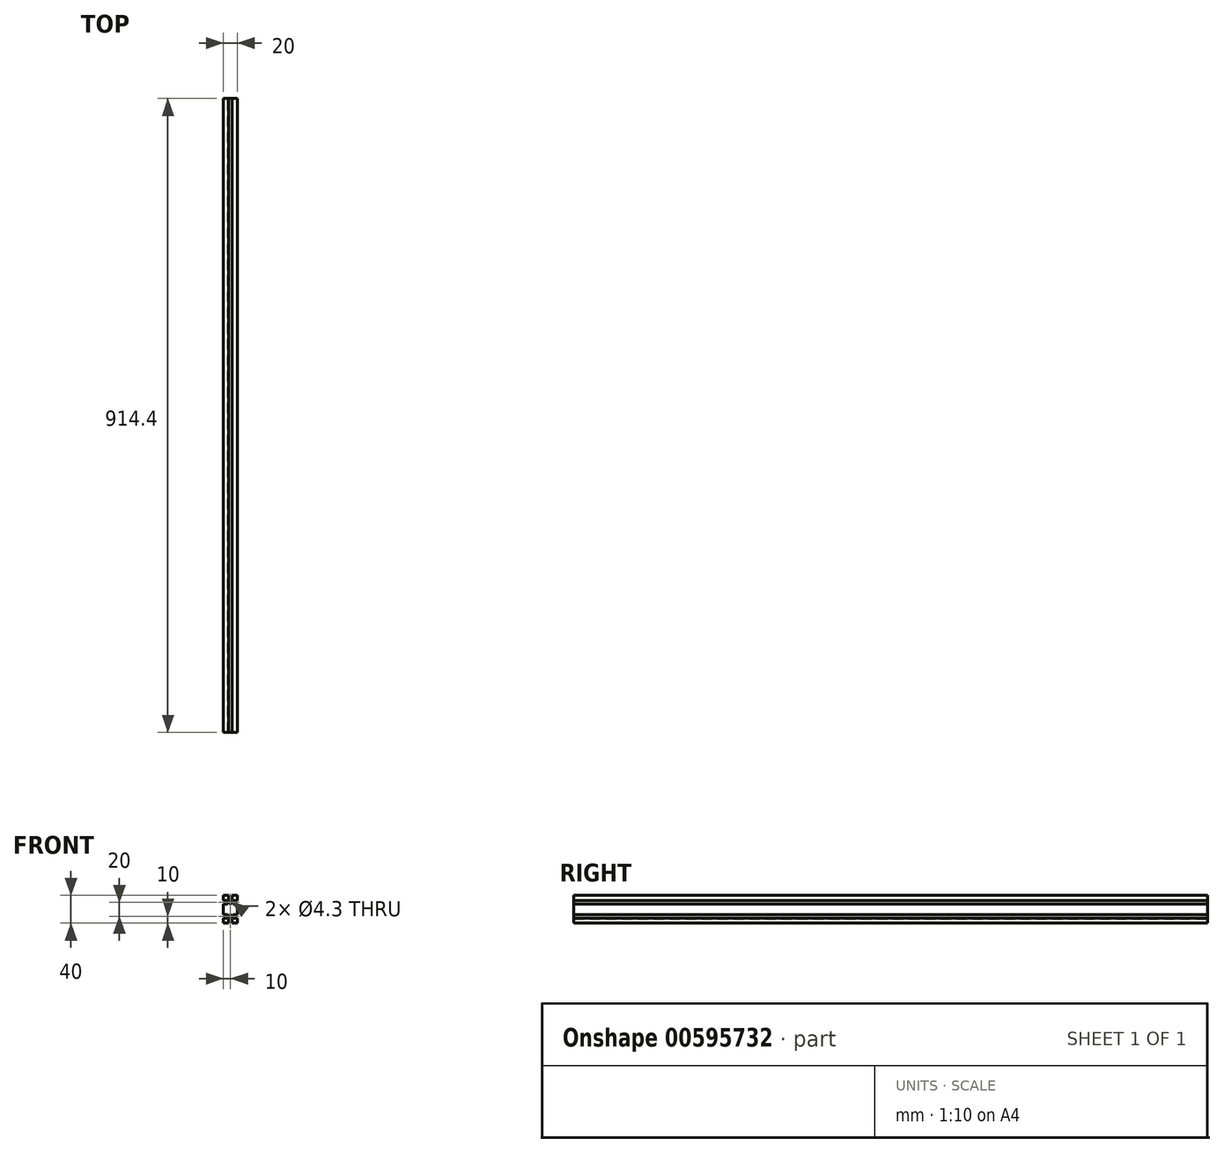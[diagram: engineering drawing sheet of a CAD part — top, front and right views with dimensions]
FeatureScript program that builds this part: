
annotation { "Feature Type Name" : "Feature", "Feature Type Description" : "" }
export const myFeature = defineFeature(function(context is Context, id is Id, definition is map)
    precondition{}
    {
        {
            var Q0;
            Q0=qCreatedBy(makeId("Front.planeOp"),FACE);
            var sketch = newSketch(context, id + "F0", { "sketchPlane" : qUnion([Q0])});
            skLineSegment(sketch, "E0.bottom", {"start": v(10, -20) * mm, "end": v(-10, -20) * mm, "construction": true});
            skLineSegment(sketch, "E0.top", {"start": v(10, 20) * mm, "end": v(-10, 20) * mm, "construction": true});
            skLineSegment(sketch, "E0.left", {"start": v(10, -20) * mm, "end": v(10, 20) * mm, "construction": true});
            skLineSegment(sketch, "E0.right", {"start": v(-10, -20) * mm, "end": v(-10, 20) * mm, "construction": true});
            skPoint(sketch, "E0.middle", {"position": v(0, 0) * mm});
            skCircle(sketch, "E1", {"center": v(0, 10) * mm, "radius": 2.15 * mm});
            skLineSegment(sketch, "E2", {"start": v(-10, 0) * mm, "end": v(-10, 7.5) * mm});
            skLineSegment(sketch, "E3", {"start": v(-10, 7.5) * mm, "end": v(-3.95, 7.5) * mm});
            skLineSegment(sketch, "E4", {"start": v(-3.95, 7.5) * mm, "end": v(-3.95, 12.5) * mm});
            skLineSegment(sketch, "E5", {"start": v(-3.95, 12.5) * mm, "end": v(-10, 12.5) * mm});
            skLineSegment(sketch, "E6", {"start": v(-10, 12.5) * mm, "end": v(-10, 20) * mm});
            skLineSegment(sketch, "E7", {"start": v(-2.5, 20) * mm, "end": v(-2.5, 13.95) * mm});
            skLineSegment(sketch, "E8", {"start": v(-2.5, 13.95) * mm, "end": v(2.5, 13.95) * mm});
            skLineSegment(sketch, "E9", {"start": v(2.5, 13.95) * mm, "end": v(2.5, 20) * mm});
            skLineSegment(sketch, "E10", {"start": v(2.5, 20) * mm, "end": v(10, 20) * mm});
            skLineSegment(sketch, "E11", {"start": v(10, 12.5) * mm, "end": v(3.95, 12.5) * mm});
            skLineSegment(sketch, "E12", {"start": v(3.95, 12.5) * mm, "end": v(3.95, 7.5) * mm});
            skLineSegment(sketch, "E13", {"start": v(3.95, 7.5) * mm, "end": v(10, 7.5) * mm});
            skLineSegment(sketch, "E14", {"start": v(10, 7.5) * mm, "end": v(10, 0) * mm});
            skPoint(sketch, "E15", {"position": v(0, 13.95) * mm});
            skPoint(sketch, "E16", {"position": v(-3.95, 10) * mm});
            skPoint(sketch, "E17", {"position": v(3.95, 10) * mm});
            skLineSegment(sketch, "E18", {"start": v(-3.95, 10) * mm, "end": v(3.95, 10) * mm, "construction": true});
            skLineSegment(sketch, "E19", {"start": v(0, 13.95) * mm, "end": v(0, 0) * mm, "construction": true});
            skCircle(sketch, "E20", {"center": v(0, 10) * mm, "radius": 3.95 * mm, "construction": true});
            skLineSegment(sketch, "E21", {"start": v(10, 20) * mm, "end": v(10, 12.5) * mm});
            skLineSegment(sketch, "E22", {"start": v(-10, 20) * mm, "end": v(-2.5, 20) * mm});
            skLineSegment(sketch, "E23.MirrorCS", {"start": v(3.95, -7.5) * mm, "end": v(10, -7.5) * mm});
            skPoint(sketch, "E24.MirrorP", {"position": v(3.95, -10) * mm});
            skLineSegment(sketch, "E25.MirrorCS", {"start": v(3.95, -12.5) * mm, "end": v(3.95, -7.5) * mm});
            skLineSegment(sketch, "E26.MirrorCS", {"start": v(10, -12.5) * mm, "end": v(3.95, -12.5) * mm});
            skLineSegment(sketch, "E27.MirrorCS", {"start": v(-3.95, -10) * mm, "end": v(3.95, -10) * mm, "construction": true});
            skLineSegment(sketch, "E28.MirrorCS", {"start": v(0, -13.95) * mm, "end": v(0, 0) * mm, "construction": true});
            skPoint(sketch, "E29.MirrorP", {"position": v(-3.95, -10) * mm});
            skLineSegment(sketch, "E30.MirrorCS", {"start": v(10, -7.5) * mm, "end": v(10, 0) * mm});
            skLineSegment(sketch, "E31.MirrorCS", {"start": v(2.5, -20) * mm, "end": v(10, -20) * mm});
            skCircle(sketch, "E32.MirrorC", {"center": v(0, -10) * mm, "radius": 3.95 * mm, "construction": true});
            skLineSegment(sketch, "E33.MirrorCS", {"start": v(-10, -20) * mm, "end": v(-2.5, -20) * mm});
            skCircle(sketch, "E34.MirrorC", {"center": v(0, -10) * mm, "radius": 2.15 * mm});
            skLineSegment(sketch, "E35.MirrorCS", {"start": v(2.5, -13.95) * mm, "end": v(2.5, -20) * mm});
            skLineSegment(sketch, "E36.MirrorCS", {"start": v(-2.5, -13.95) * mm, "end": v(2.5, -13.95) * mm});
            skPoint(sketch, "E37.MirrorP", {"position": v(0, -13.95) * mm});
            skLineSegment(sketch, "E38.MirrorCS", {"start": v(-10, -7.5) * mm, "end": v(-3.95, -7.5) * mm});
            skLineSegment(sketch, "E39.MirrorCS", {"start": v(-10, 0) * mm, "end": v(-10, -7.5) * mm});
            skLineSegment(sketch, "E40.MirrorCS", {"start": v(10, -20) * mm, "end": v(10, -12.5) * mm});
            skLineSegment(sketch, "E41.MirrorCS", {"start": v(-3.95, -12.5) * mm, "end": v(-10, -12.5) * mm});
            skLineSegment(sketch, "E42.MirrorCS", {"start": v(-3.95, -7.5) * mm, "end": v(-3.95, -12.5) * mm});
            skLineSegment(sketch, "E43.MirrorCS", {"start": v(-10, -12.5) * mm, "end": v(-10, -20) * mm});
            skLineSegment(sketch, "E44.MirrorCS", {"start": v(-2.5, -20) * mm, "end": v(-2.5, -13.95) * mm});
            skSolve(sketch);
        }
        {
            var Q0;
            Q0=makeQuery(id+"F0.imprint","IMPRINT",FACE,{"disambiguationData":[TD([[makeQuery(id+"F0.imprint","IMPRINT",EDGE,{"derivedFrom":sQuery(id+"F0.wireOp",EDGE,"E1")}),-1.0]])]});
            extrude(context, id + "F1", {"entities" : qUnion([Q0]), "depth" : 914.4 * mm, "offsetDistance" : 25 * mm, "symmetric" : true});
        }
    });
